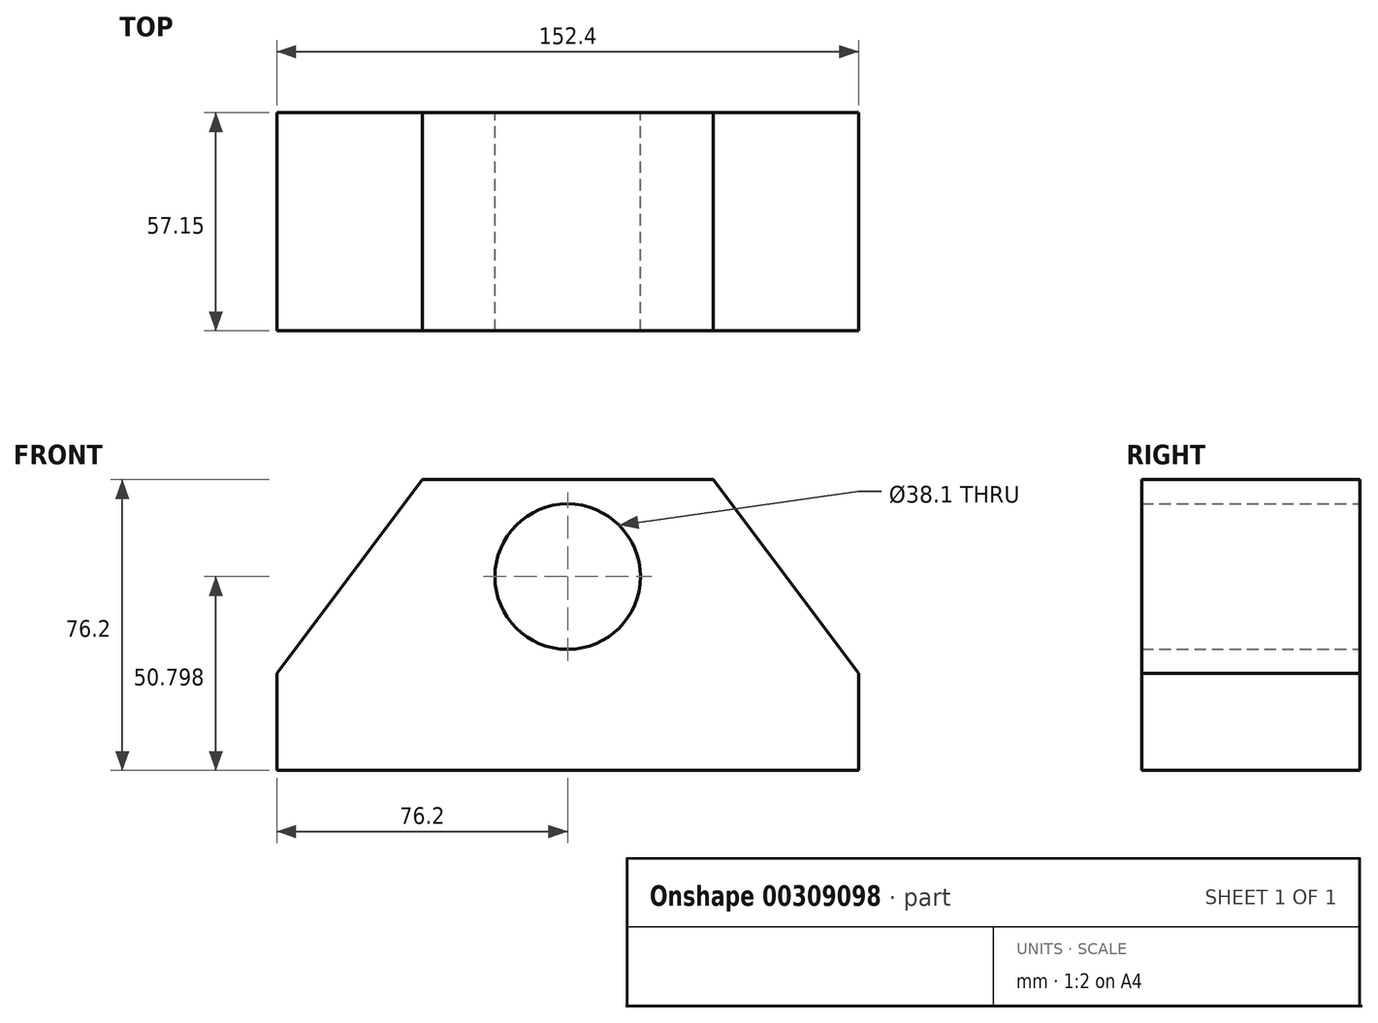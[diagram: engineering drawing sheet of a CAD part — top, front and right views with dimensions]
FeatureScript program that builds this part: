
annotation { "Feature Type Name" : "Feature", "Feature Type Description" : "" }
export const myFeature = defineFeature(function(context is Context, id is Id, definition is map)
    precondition{}
    {
        {
            var Q0;
            Q0=qCreatedBy(makeId("Front.planeOp"),FACE);
            var sketch = newSketch(context, id + "F0", { "sketchPlane" : qUnion([Q0])});
            skLineSegment(sketch, "E0", {"start": v(-38.1, 33.87) * mm, "end": v(38.1, 33.87) * mm});
            skLineSegment(sketch, "E1", {"start": v(38.1, 33.87) * mm, "end": v(76.2, -16.93) * mm});
            skLineSegment(sketch, "E2", {"start": v(76.2, -16.93) * mm, "end": v(76.2, -42.33) * mm});
            skLineSegment(sketch, "E3", {"start": v(76.2, -42.33) * mm, "end": v(-76.2, -42.33) * mm});
            skLineSegment(sketch, "E4", {"start": v(-76.2, -42.33) * mm, "end": v(-76.2, -16.93) * mm});
            skLineSegment(sketch, "E5", {"start": v(-76.2, -16.93) * mm, "end": v(-38.1, 33.87) * mm});
            skCircle(sketch, "E6", {"center": v(0, 8.47) * mm, "radius": 19.05 * mm});
            skSolve(sketch);
        }
        {
            var Q0;
            Q0 = qSketchRegion(id + "F0", true);
            extrude(context, id + "F1", {"entities" : qUnion([Q0]), "depth" : 57.15 * mm});
        }
    });
